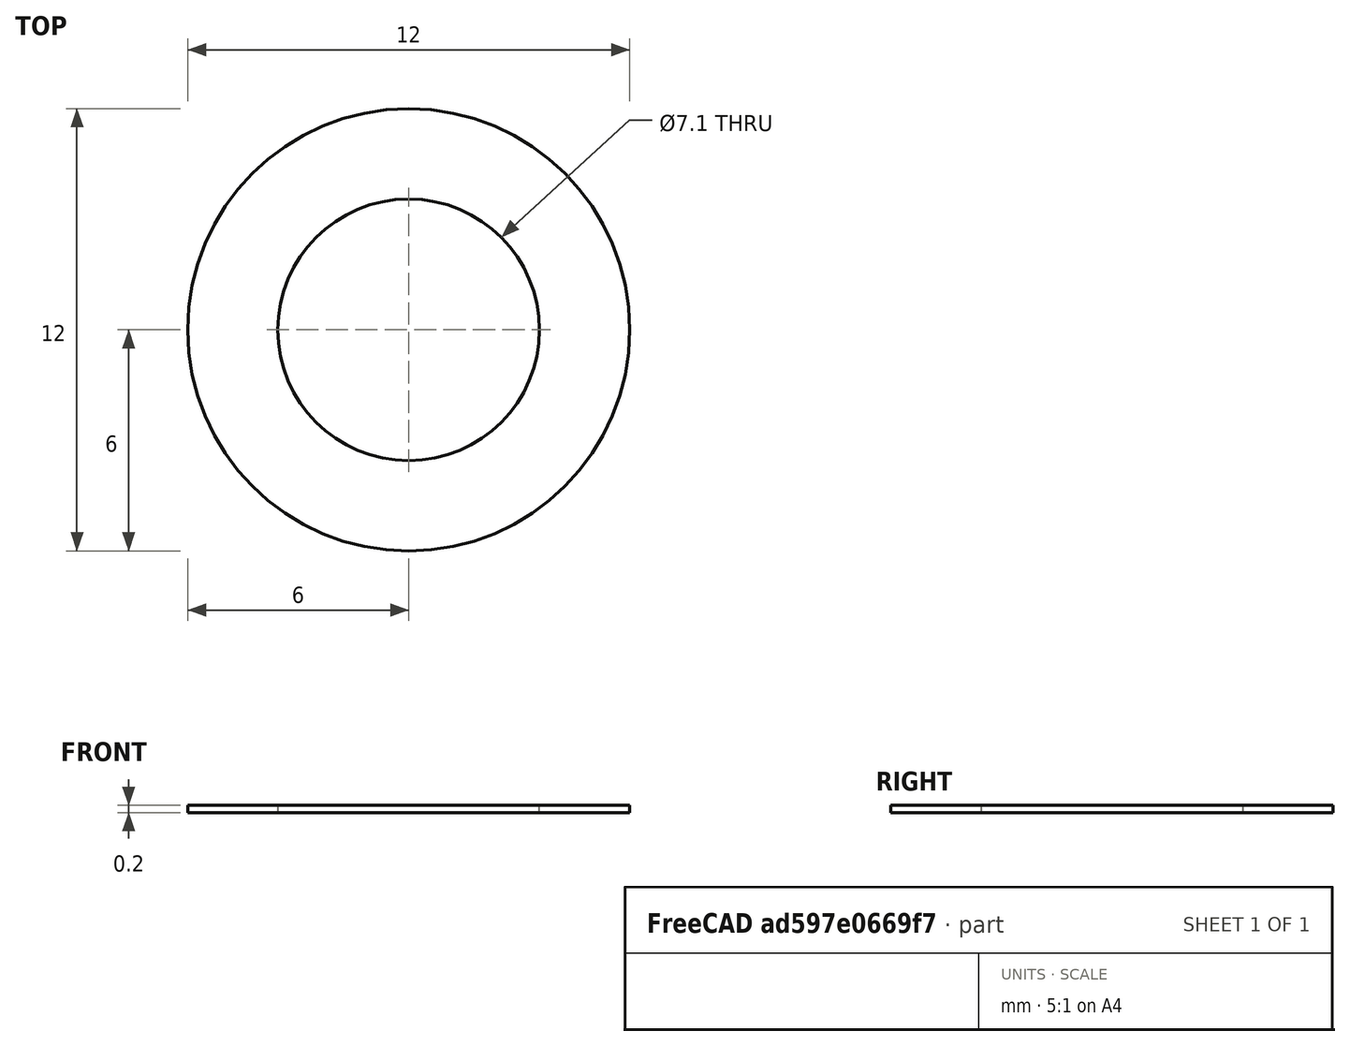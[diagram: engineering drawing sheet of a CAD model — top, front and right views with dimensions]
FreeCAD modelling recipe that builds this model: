
FCSTD DOCUMENT  (FreeCAD 0.19R16699 (Git))
Label: Washer_M7.1x0.2mm
License: All rights reserved
LicenseURL: http://en.wikipedia.org/wiki/All_rights_reserved
objects: Sketcher::SketchObject×1, PartDesign::Pad×1, PartDesign::Body×1
note: 4 computed .brp shape members not serialized (recipe doc carries the construction recipe); baked Part::Feature solids carry a one-line shape summary decoded from their .brp

FEATURE [Sketcher::SketchObject] Sketch
  MapMode = 5
  Support = -> [XY_Plane]
  sketch-geometry (2):
    g0: Circle CenterX=0 CenterY=0 CenterZ=0 NormalX=0 NormalY=0 NormalZ=1 AngleXU=0 Radius=3.55
    g1: Circle CenterX=0 CenterY=0 CenterZ=0 NormalX=0 NormalY=0 NormalZ=1 AngleXU=0 Radius=6
  constraints (4):
    c: Coincident(g0,g-1)
    c: Coincident(g1,g0)
    c: Radius(g0) = 3.55
    c: Radius(g1) = 6
FEATURE [PartDesign::Pad] Pad
  Length = 0.2
  Length2 = 100
  Profile = -> Sketch
  Type = 0
FEATURE [PartDesign::Body] Body
  Group = -> [Sketch,Pad]
  Origin = -> Origin
  Tip = -> Pad
